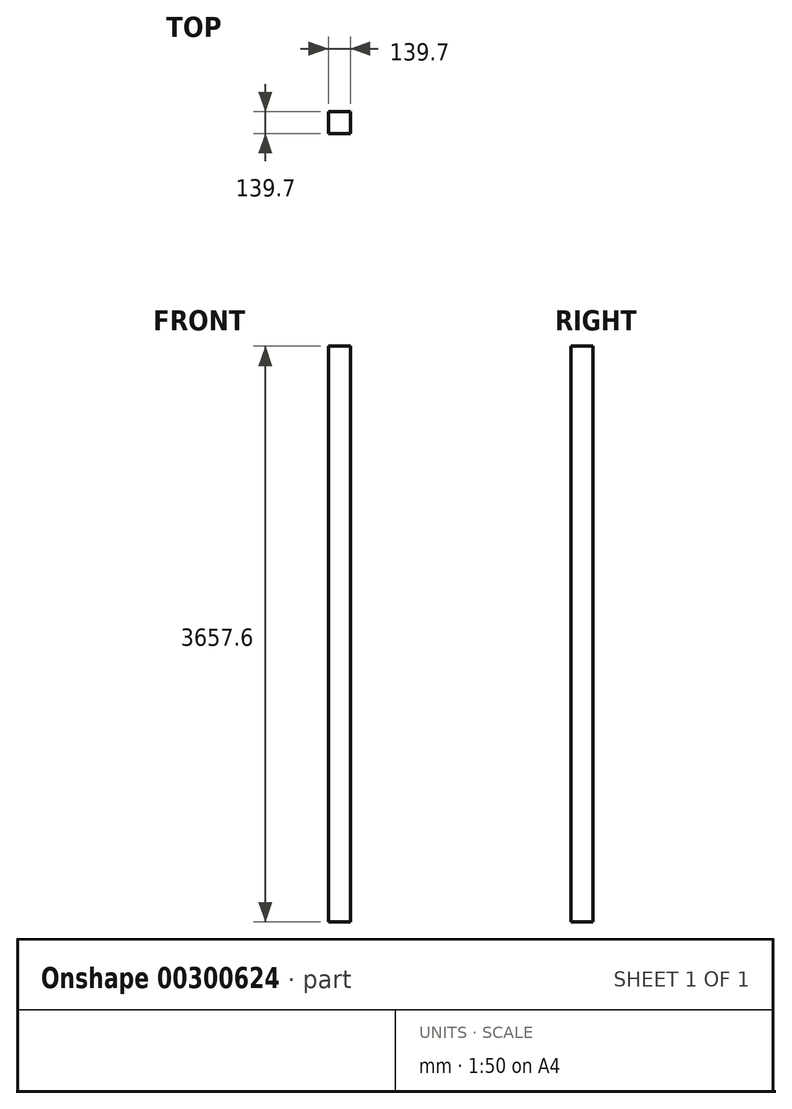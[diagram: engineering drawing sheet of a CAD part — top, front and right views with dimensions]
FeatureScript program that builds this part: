
annotation { "Feature Type Name" : "Feature", "Feature Type Description" : "" }
export const myFeature = defineFeature(function(context is Context, id is Id, definition is map)
    precondition{}
    {
        {
            var Q0;
            Q0=qCreatedBy(makeId("Top.planeOp"),FACE);
            var sketch = newSketch(context, id + "F0", { "sketchPlane" : qUnion([Q0])});
            skLineSegment(sketch, "E0.bottom", {"start": v(0, 0) * mm, "end": v(139.7, 0) * mm});
            skLineSegment(sketch, "E0.top", {"start": v(0, 139.7) * mm, "end": v(139.7, 139.7) * mm});
            skLineSegment(sketch, "E0.left", {"start": v(0, 0) * mm, "end": v(0, 139.7) * mm});
            skLineSegment(sketch, "E0.right", {"start": v(139.7, 0) * mm, "end": v(139.7, 139.7) * mm});
            skSolve(sketch);
        }
        {
            var Q0;
            Q0 = qSketchRegion(id + "F0", true);
            extrude(context, id + "F1", {"entities" : qUnion([Q0]), "depth" : 3657.6 * mm});
        }
    });
